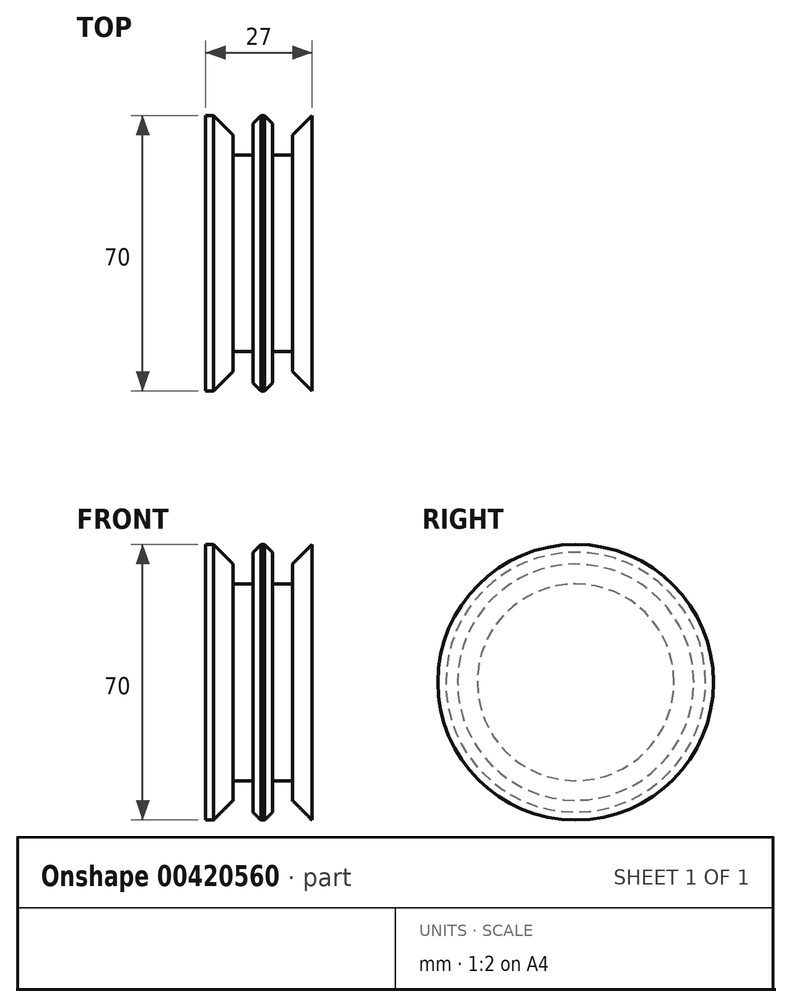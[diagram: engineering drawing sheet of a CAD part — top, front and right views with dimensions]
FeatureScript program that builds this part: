
annotation { "Feature Type Name" : "Feature", "Feature Type Description" : "" }
export const myFeature = defineFeature(function(context is Context, id is Id, definition is map)
    precondition{}
    {
        {
            var Q0;
            Q0=qCreatedBy(makeId("Right.planeOp"),FACE);
            var sketch = newSketch(context, id + "F0", { "sketchPlane" : qUnion([Q0])});
            skCircle(sketch, "E0", {"center": v(0, 0) * mm, "radius": 35 * mm});
            skSolve(sketch);
        }
        {
            var Q0;
            Q0 = qSketchRegion(id + "F0", true);
            extrude(context, id + "F1", {"entities" : qUnion([Q0]), "depth" : 7 * mm});
        }
        {
            var Q0;
            Q0=makeQuery(id+"F1.opExtrude","CAP_FACE",FACE,{"disambiguationData":[OSD([sQuery(id+"F0.wireOp",EDGE,"E0")])],"isStart":false});
            var sketch = newSketch(context, id + "F2", { "sketchPlane" : qUnion([Q0])});
            skCircle(sketch, "E1", {"center": v(0, 0) * mm, "radius": 25 * mm});
            skSolve(sketch);
        }
        {
            var Q0;
            Q0 = qSketchRegion(id + "F2", true);
            extrude(context, id + "F3", {"entities" : qUnion([Q0]), "operationType" : NewBodyOperationType.ADD, "depth" : 5 * mm});
        }
        {
            var Q0;
            Q0=makeQuery(id+"F3.opExtrude","CAP_FACE",FACE,{"disambiguationData":[OSD([sQuery(id+"F2.wireOp",EDGE,"E1")])],"isStart":false});
            var sketch = newSketch(context, id + "F4", { "sketchPlane" : qUnion([Q0])});
            skSolve(sketch);
        }
        {
            var Q0;
            Q0=makeQuery(id+"F4.imprint","IMPRINT",FACE,{"disambiguationData":[TD([[makeQuery(id+"F4.imprint","IMPRINT",EDGE,{"derivedFrom":makeQuery(id+"F3.opExtrude","CAP_EDGE",EDGE,{"disambiguationData":[OSD([sQuery(id+"F2.wireOp",EDGE,"E1")])],"isStart":false})}),1.0]])]});
            var sketch = newSketch(context, id + "F5", { "sketchPlane" : qUnion([Q0])});
            skCircle(sketch, "E2", {"center": v(0, 0) * mm, "radius": 35 * mm});
            skSolve(sketch);
        }
        {
            var Q0;
            Q0 = qSketchRegion(id + "F5", true);
            extrude(context, id + "F6", {"entities" : qUnion([Q0]), "operationType" : NewBodyOperationType.ADD, "depth" : 5 * mm});
        }
        {
            var Q0;
            Q0=makeQuery(id+"F6.opExtrude","CAP_FACE",FACE,{"disambiguationData":[OSD([sQuery(id+"F5.wireOp",EDGE,"E2")])],"isStart":false});
            var sketch = newSketch(context, id + "F7", { "sketchPlane" : qUnion([Q0])});
            skCircle(sketch, "E3", {"center": v(0, 0) * mm, "radius": 25 * mm});
            skSolve(sketch);
        }
        {
            var Q0;
            Q0=makeQuery(id+"F7.imprint","IMPRINT",FACE,{"disambiguationData":[TD([[makeQuery(id+"F7.imprint","IMPRINT",EDGE,{"derivedFrom":sQuery(id+"F7.wireOp",EDGE,"E3")}),1.0]])]});
            extrude(context, id + "F8", {"entities" : qUnion([Q0]), "operationType" : NewBodyOperationType.ADD, "depth" : 5 * mm});
        }
        {
            var Q0;
            Q0=makeQuery(id+"F8.opExtrude","CAP_FACE",FACE,{"disambiguationData":[OSD([sQuery(id+"F7.wireOp",EDGE,"E3")])],"isStart":false});
            var sketch = newSketch(context, id + "F9", { "sketchPlane" : qUnion([Q0])});
            skCircle(sketch, "E4", {"center": v(0, 0) * mm, "radius": 35 * mm});
            skSolve(sketch);
        }
        {
            var Q0;
            Q0 = qSketchRegion(id + "F9", true);
            extrude(context, id + "F10", {"entities" : qUnion([Q0]), "operationType" : NewBodyOperationType.ADD, "depth" : 5 * mm});
        }
        {
            var Q0;
            Q0=makeQuery(id+"F1.opExtrude","CAP_EDGE",EDGE,{"disambiguationData":[OSD([sQuery(id+"F0.wireOp",EDGE,"E0")])],"isStart":false});
            var Q1;
            Q1=makeQuery(id+"F10.opExtrude","CAP_EDGE",EDGE,{"disambiguationData":[OSD([sQuery(id+"F9.wireOp",EDGE,"E4")])],"isStart":true});
            chamfer(context, id + "F11", {"entities" : qUnion([Q0, Q1]), "width" : 5 * mm, "tangentPropagation" : true});
        }
        {
            var Q0;
            Q0=makeQuery(id+"F6.opExtrude","CAP_EDGE",EDGE,{"disambiguationData":[OSD([sQuery(id+"F5.wireOp",EDGE,"E2")])],"isStart":true});
            var Q1;
            Q1=makeQuery(id+"F6.opExtrude","CAP_EDGE",EDGE,{"disambiguationData":[OSD([sQuery(id+"F5.wireOp",EDGE,"E2")])],"isStart":false});
            chamfer(context, id + "F12", {"entities" : qUnion([Q0, Q1]), "width" : 2 * mm, "tangentPropagation" : true});
        }
    });
